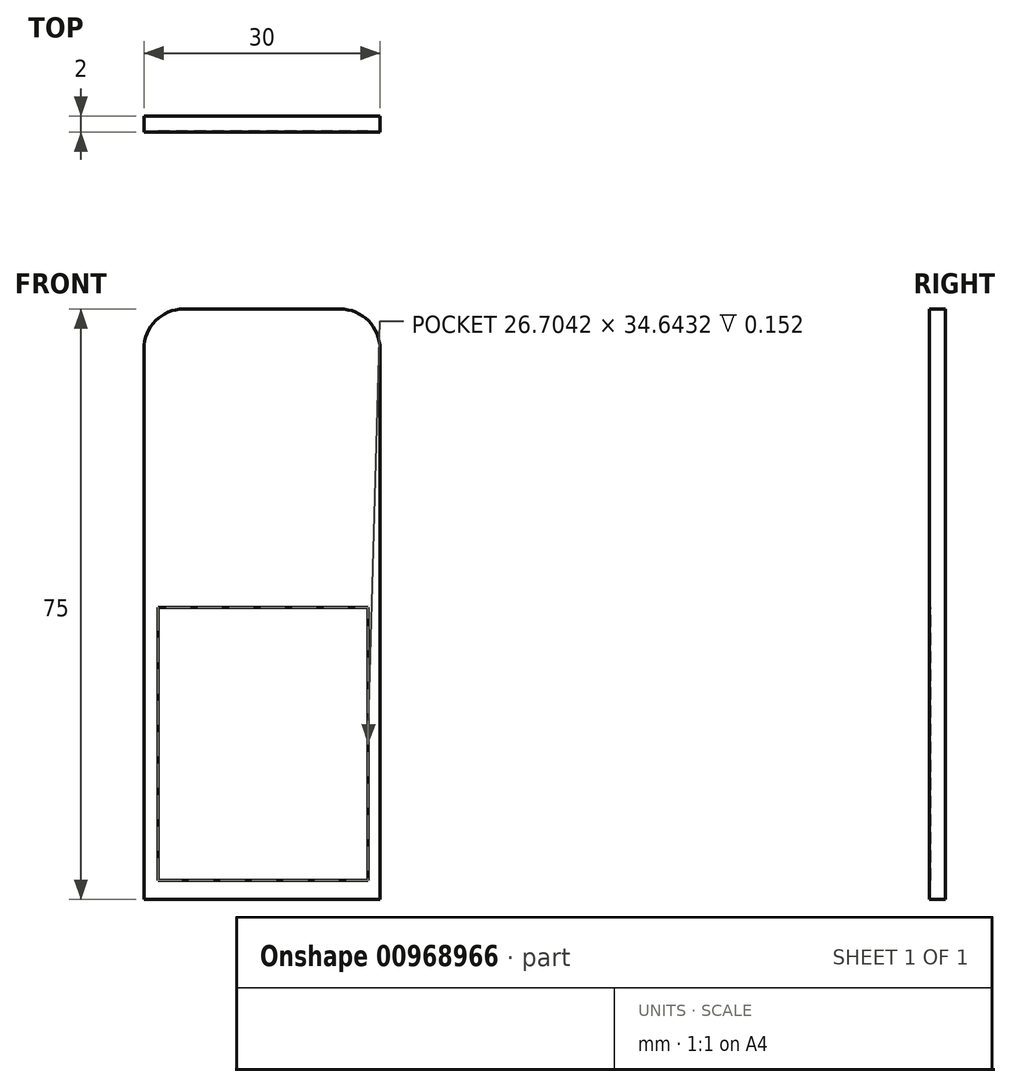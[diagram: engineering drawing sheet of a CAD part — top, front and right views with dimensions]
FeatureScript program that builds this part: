
annotation { "Feature Type Name" : "Feature", "Feature Type Description" : "" }
export const myFeature = defineFeature(function(context is Context, id is Id, definition is map)
    precondition{}
    {
        {
            var Q0;
            Q0=qCreatedBy(makeId("Front.planeOp"),FACE);
            var sketch = newSketch(context, id + "F0", { "sketchPlane" : qUnion([Q0])});
            skLineSegment(sketch, "E0.bottom", {"start": v(0, 0) * mm, "end": v(30, 0) * mm});
            skLineSegment(sketch, "E0.top", {"start": v(0, 75) * mm, "end": v(30, 75) * mm});
            skLineSegment(sketch, "E0.left", {"start": v(0, 0) * mm, "end": v(0, 75) * mm});
            skLineSegment(sketch, "E0.right", {"start": v(30, 0) * mm, "end": v(30, 75) * mm});
            skSolve(sketch);
        }
        {
            var Q0;
            Q0 = qSketchRegion(id + "F0", true);
            extrude(context, id + "F1", {"entities" : qUnion([Q0]), "depth" : 2 * mm, "offsetDistance" : 25.4 * mm});
        }
        {
            var Q0;
            Q0=makeQuery(id+"F1.opExtrude","SWEPT_EDGE",EDGE,{"disambiguationData":[OSD([sQuery(id+"F0.wireOp",EDGE,"E0.top"),sQuery(id+"F0.wireOp",EDGE,"E0.right")])]});
            var Q1;
            Q1=makeQuery(id+"F1.opExtrude","SWEPT_EDGE",EDGE,{"disambiguationData":[OSD([sQuery(id+"F0.wireOp",EDGE,"E0.top"),sQuery(id+"F0.wireOp",EDGE,"E0.left")])]});
            fillet(context, id + "F2", {"entities" : qUnion([Q0, Q1]), "radius" : 5.08 * mm, "tangentPropagation" : true, "allowEdgeOverflow" : false});
        }
        {
            var Q0;
            Q0=makeQuery(id+"F1.opExtrude","CAP_FACE",FACE,{"disambiguationData":[OSD([sQuery(id+"F0.wireOp",EDGE,"E0.bottom"),sQuery(id+"F0.wireOp",EDGE,"E0.top"),sQuery(id+"F0.wireOp",EDGE,"E0.left"),sQuery(id+"F0.wireOp",EDGE,"E0.right")])],"isStart":false});
            var sketch = newSketch(context, id + "F3", { "sketchPlane" : qUnion([Q0])});
            skLineSegment(sketch, "E1.bottom", {"start": v(1.77, 2.42) * mm, "end": v(28.48, 2.42) * mm});
            skLineSegment(sketch, "E1.top", {"start": v(1.77, 37.06) * mm, "end": v(28.48, 37.06) * mm});
            skLineSegment(sketch, "E1.left", {"start": v(1.77, 2.42) * mm, "end": v(1.77, 37.06) * mm});
            skLineSegment(sketch, "E1.right", {"start": v(28.48, 2.42) * mm, "end": v(28.48, 37.06) * mm});
            skSolve(sketch);
        }
        {
            var Q0;
            Q0 = qSketchRegion(id + "F3", true);
            extrude(context, id + "F4", {"entities" : qUnion([Q0]), "operationType" : NewBodyOperationType.REMOVE, "oppositeDirection" : true, "depth" : 0.15 * mm, "offsetDistance" : 25.4 * mm});
        }
    });
